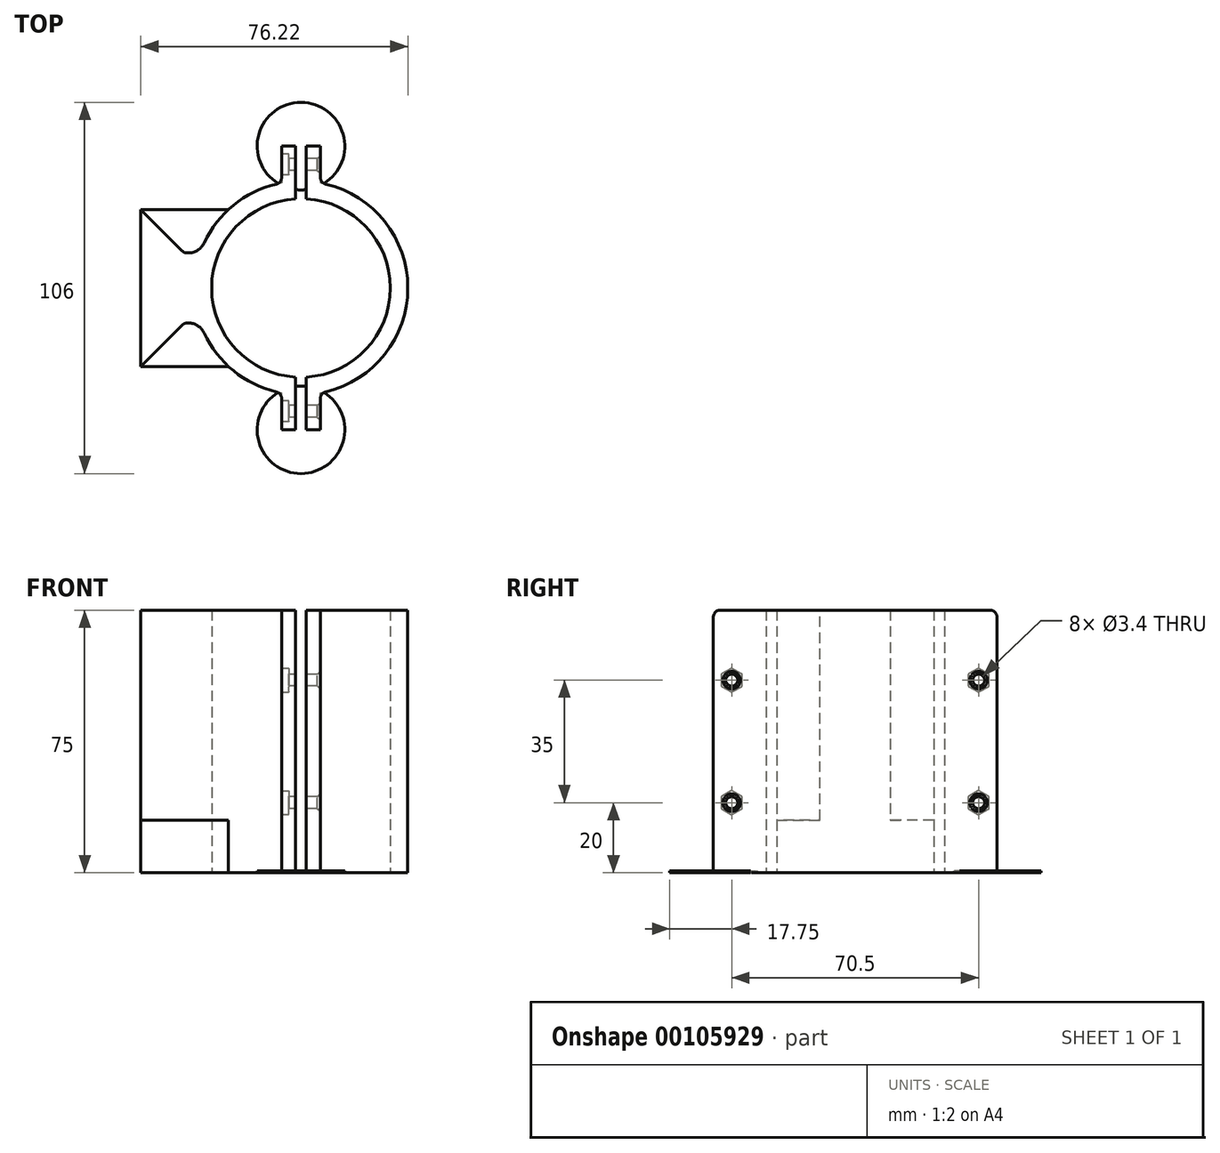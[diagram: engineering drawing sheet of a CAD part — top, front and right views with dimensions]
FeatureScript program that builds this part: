
annotation { "Feature Type Name" : "Feature", "Feature Type Description" : "" }
export const myFeature = defineFeature(function(context is Context, id is Id, definition is map)
    precondition{}
    {
        {
            var Q0;
            Q0=qCreatedBy(makeId("Top.planeOp"),FACE);
            var sketch = newSketch(context, id + "F11", { "sketchPlane" : qUnion([Q0])});
            skLineSegment(sketch, "E0", {"start": v(-5.55, -72.11) * mm, "end": v(110.36, -72.11) * mm, "construction": true});
            skLineSegment(sketch, "E1", {"start": v(-5.55, -72.11) * mm, "end": v(-5.55, -49.71) * mm});
            skLineSegment(sketch, "E2", {"start": v(-5.55, -49.71) * mm, "end": v(6.85, -62.11) * mm});
            skLineSegment(sketch, "E3", {"start": v(6.85, -62.11) * mm, "end": v(11.35, -62.11) * mm});
            skLineSegment(sketch, "E4", {"start": v(11.35, -62.11) * mm, "end": v(11.35, -72.11) * mm});
            skLineSegment(sketch, "E5.MirrorCS", {"start": v(-5.55, -94.51) * mm, "end": v(6.85, -82.11) * mm});
            skLineSegment(sketch, "E6.MirrorCS", {"start": v(11.35, -82.11) * mm, "end": v(11.35, -72.11) * mm});
            skLineSegment(sketch, "E7.MirrorCS", {"start": v(6.85, -82.11) * mm, "end": v(11.35, -82.11) * mm});
            skLineSegment(sketch, "E8.MirrorCS", {"start": v(-5.55, -72.11) * mm, "end": v(-5.55, -94.51) * mm});
            skCircle(sketch, "E9", {"center": v(40.17, -72.11) * mm, "radius": 30.5 * mm});
            skCircle(sketch, "E10.0", {"center": v(40.17, -72.11) * mm, "radius": 25.5 * mm});
            skLineSegment(sketch, "E11", {"start": v(40.17, -31.61) * mm, "end": v(40.17, -110.67) * mm, "construction": true});
            skLineSegment(sketch, "E12", {"start": v(38.67, -31.61) * mm, "end": v(38.67, -46.65) * mm});
            skLineSegment(sketch, "E13", {"start": v(38.67, -31.61) * mm, "end": v(34.67, -31.61) * mm});
            skLineSegment(sketch, "E14", {"start": v(34.67, -31.61) * mm, "end": v(34.67, -47.21) * mm});
            skLineSegment(sketch, "E15.MirrorCS", {"start": v(41.67, -31.61) * mm, "end": v(41.67, -46.65) * mm});
            skLineSegment(sketch, "E16.MirrorCS", {"start": v(45.67, -31.61) * mm, "end": v(45.67, -47.21) * mm});
            skLineSegment(sketch, "E17.MirrorCS", {"start": v(41.67, -31.61) * mm, "end": v(45.67, -31.61) * mm});
            skLineSegment(sketch, "E18.MirrorCS", {"start": v(34.67, -112.61) * mm, "end": v(34.67, -97.01) * mm});
            skLineSegment(sketch, "E19.MirrorCS", {"start": v(41.67, -112.61) * mm, "end": v(45.67, -112.61) * mm});
            skLineSegment(sketch, "E20.MirrorCS", {"start": v(38.67, -112.61) * mm, "end": v(34.67, -112.61) * mm});
            skLineSegment(sketch, "E21.MirrorCS", {"start": v(41.67, -112.61) * mm, "end": v(41.67, -97.57) * mm});
            skLineSegment(sketch, "E22.MirrorCS", {"start": v(45.67, -112.61) * mm, "end": v(45.67, -97.01) * mm});
            skLineSegment(sketch, "E23.MirrorCS", {"start": v(38.67, -112.61) * mm, "end": v(38.67, -97.57) * mm});
            skLineSegment(sketch, "E24", {"start": v(-5.55, -49.71) * mm, "end": v(19.47, -49.71) * mm});
            skLineSegment(sketch, "E25", {"start": v(-5.55, -94.51) * mm, "end": v(19.47, -94.51) * mm});
            skCircle(sketch, "E26", {"center": v(40.17, -31.61) * mm, "radius": 12.5 * mm});
            skCircle(sketch, "E27.MirrorC", {"center": v(40.17, -112.61) * mm, "radius": 12.5 * mm});
            skSolve(sketch);
        }
        {
            var Q0;
            Q0=makeQuery(id+"F11.imprint","IMPRINT",FACE,{"disambiguationData":[TD([[makeQuery(id+"F11.imprint","IMPRINT",EDGE,{"derivedFrom":sQuery(id+"F11.wireOp",EDGE,"E1")}),-1.0]])]});
            var Q1;
            {var subQ0=sQuery(id+"F11.wireOp",EDGE,"E4");Q1=makeQuery(id+"F11.imprint","IMPRINT",FACE,{"disambiguationData":[TD([[makeQuery(id+"F11.imprint","IMPRINT",EDGE,{"derivedFrom":subQ0}),-1.0]])]});}
            var Q2;
            {var subQ10=sQuery(id+"F11.wireOp",EDGE,"E4");Q2=makeQuery(id+"F11.imprint","IMPRINT",FACE,{"disambiguationData":[TD([[makeQuery(id+"F11.imprint","IMPRINT",EDGE,{"derivedFrom":subQ10}),1.0]])]});}
            var Q3;
            {var subQ5=sQuery(id+"F11.wireOp",EDGE,"E13");Q3=makeQuery(id+"F11.imprint","IMPRINT",FACE,{"disambiguationData":[TD([[makeQuery(id+"F11.imprint","IMPRINT",EDGE,{"derivedFrom":subQ5}),1.0]])]});}
            var Q4;
            {var subQ5=sQuery(id+"F11.wireOp",EDGE,"E17.MirrorCS");Q4=makeQuery(id+"F11.imprint","IMPRINT",FACE,{"disambiguationData":[TD([[makeQuery(id+"F11.imprint","IMPRINT",EDGE,{"derivedFrom":subQ5}),-1.0]])]});}
            var Q5;
            {var subQ0=sQuery(id+"F11.wireOp",EDGE,"E12");var subQ3=sQuery(id+"F11.wireOp",EDGE,"E9");var subQ4=makeQuery(id+"F11.imprint","INTERSECT",VERTEX,{"derivedFrom":[subQ3,subQ0]});Q5=makeQuery(id+"F11.imprint","IMPRINT",FACE,{"disambiguationData":[TD([[makeQuery(id+"F11.imprint","IMPRINT",EDGE,{"disambiguationData":[TD([[subQ4,-1.0]])],"derivedFrom":subQ3}),1.0]])]});}
            var Q6;
            {var subQ0=sQuery(id+"F11.wireOp",EDGE,"E16.MirrorCS");var subQ1=sQuery(id+"F11.wireOp",EDGE,"E9");var subQ2=makeQuery(id+"F11.imprint","INTERSECT",VERTEX,{"derivedFrom":[subQ1,subQ0]});Q6=makeQuery(id+"F11.imprint","IMPRINT",FACE,{"disambiguationData":[TD([[makeQuery(id+"F11.imprint","IMPRINT",EDGE,{"disambiguationData":[TD([[subQ2,-1.0]])],"derivedFrom":subQ1}),1.0]])]});}
            var Q7;
            {var subQ0=sQuery(id+"F11.wireOp",EDGE,"E26");var subQ1=sQuery(id+"F11.wireOp",EDGE,"E9");var subQ2=makeQuery(id+"F11.imprint","INTERSECT",VERTEX,{"disambiguationData":[OD(0.0)],"derivedFrom":[subQ1,subQ0]});Q7=makeQuery(id+"F11.imprint","IMPRINT",FACE,{"disambiguationData":[TD([[makeQuery(id+"F11.imprint","IMPRINT",EDGE,{"disambiguationData":[TD([[subQ2,-1.0]])],"derivedFrom":subQ1}),1.0]])]});}
            var Q8;
            {var subQ7=sQuery(id+"F11.wireOp",EDGE,"E26");var subQ9=sQuery(id+"F11.wireOp",EDGE,"E9");var subQ10=makeQuery(id+"F11.imprint","INTERSECT",VERTEX,{"disambiguationData":[OD(0.0)],"derivedFrom":[subQ9,subQ7]});Q8=makeQuery(id+"F11.imprint","IMPRINT",FACE,{"disambiguationData":[TD([[makeQuery(id+"F11.imprint","IMPRINT",EDGE,{"disambiguationData":[TD([[subQ10,1.0]])],"derivedFrom":subQ9}),1.0]])]});}
            var Q9;
            {var subQ0=sQuery(id+"F11.wireOp",EDGE,"E26");var subQ1=sQuery(id+"F11.wireOp",EDGE,"E9");var subQ2=makeQuery(id+"F11.imprint","INTERSECT",VERTEX,{"disambiguationData":[OD(1.0)],"derivedFrom":[subQ1,subQ0]});Q9=makeQuery(id+"F11.imprint","IMPRINT",FACE,{"disambiguationData":[TD([[makeQuery(id+"F11.imprint","IMPRINT",EDGE,{"disambiguationData":[TD([[subQ2,1.0]])],"derivedFrom":subQ1}),1.0]])]});}
            var Q10;
            {var subQ0=sQuery(id+"F11.wireOp",EDGE,"E27.MirrorC");var subQ1=sQuery(id+"F11.wireOp",EDGE,"E9");var subQ2=makeQuery(id+"F11.imprint","INTERSECT",VERTEX,{"disambiguationData":[OD(0.0)],"derivedFrom":[subQ1,subQ0]});Q10=makeQuery(id+"F11.imprint","IMPRINT",FACE,{"disambiguationData":[TD([[makeQuery(id+"F11.imprint","IMPRINT",EDGE,{"disambiguationData":[TD([[subQ2,-1.0]])],"derivedFrom":subQ1}),1.0]])]});}
            var Q11;
            {var subQ3=sQuery(id+"F11.wireOp",EDGE,"E9");var subQ7=sQuery(id+"F11.wireOp",EDGE,"E18.MirrorCS");var subQ9=makeQuery(id+"F11.imprint","INTERSECT",VERTEX,{"derivedFrom":[subQ3,subQ7]});Q11=makeQuery(id+"F11.imprint","IMPRINT",FACE,{"disambiguationData":[TD([[makeQuery(id+"F11.imprint","IMPRINT",EDGE,{"disambiguationData":[TD([[subQ9,-1.0]])],"derivedFrom":subQ3}),1.0]])]});}
            var Q12;
            {var subQ5=sQuery(id+"F11.wireOp",EDGE,"E20.MirrorCS");Q12=makeQuery(id+"F11.imprint","IMPRINT",FACE,{"disambiguationData":[TD([[makeQuery(id+"F11.imprint","IMPRINT",EDGE,{"derivedFrom":subQ5}),-1.0]])]});}
            var Q13;
            {var subQ0=sQuery(id+"F11.wireOp",EDGE,"E27.MirrorC");var subQ1=sQuery(id+"F11.wireOp",EDGE,"E9");var subQ2=makeQuery(id+"F11.imprint","INTERSECT",VERTEX,{"disambiguationData":[OD(1.0)],"derivedFrom":[subQ1,subQ0]});Q13=makeQuery(id+"F11.imprint","IMPRINT",FACE,{"disambiguationData":[TD([[makeQuery(id+"F11.imprint","IMPRINT",EDGE,{"disambiguationData":[TD([[subQ2,1.0]])],"derivedFrom":subQ1}),1.0]])]});}
            var Q14;
            {var subQ1=sQuery(id+"F11.wireOp",EDGE,"E9");var subQ5=sQuery(id+"F11.wireOp",EDGE,"E21.MirrorCS");var subQ8=makeQuery(id+"F11.imprint","INTERSECT",VERTEX,{"derivedFrom":[subQ1,subQ5]});Q14=makeQuery(id+"F11.imprint","IMPRINT",FACE,{"disambiguationData":[TD([[makeQuery(id+"F11.imprint","IMPRINT",EDGE,{"disambiguationData":[TD([[subQ8,-1.0]])],"derivedFrom":subQ1}),1.0]])]});}
            var Q15;
            {var subQ5=sQuery(id+"F11.wireOp",EDGE,"E19.MirrorCS");Q15=makeQuery(id+"F11.imprint","IMPRINT",FACE,{"disambiguationData":[TD([[makeQuery(id+"F11.imprint","IMPRINT",EDGE,{"derivedFrom":subQ5}),1.0]])]});}
            var Q16;
            {var subQ0=sQuery(id+"F11.wireOp",EDGE,"E14");var subQ1=sQuery(id+"F11.wireOp",EDGE,"E10.0");var subQ2=makeQuery(id+"F11.imprint","INTERSECT",VERTEX,{"derivedFrom":[subQ1,subQ0]});Q16=makeQuery(id+"F11.imprint","IMPRINT",FACE,{"disambiguationData":[TD([[makeQuery(id+"F11.imprint","IMPRINT",EDGE,{"disambiguationData":[TD([[subQ2,1.0]])],"derivedFrom":subQ1}),-1.0]])]});}
            var Q17;
            {var subQ0=sQuery(id+"F11.wireOp",EDGE,"E16.MirrorCS");var subQ1=sQuery(id+"F11.wireOp",EDGE,"E10.0");var subQ2=makeQuery(id+"F11.imprint","INTERSECT",VERTEX,{"derivedFrom":[subQ1,subQ0]});Q17=makeQuery(id+"F11.imprint","IMPRINT",FACE,{"disambiguationData":[TD([[makeQuery(id+"F11.imprint","IMPRINT",EDGE,{"disambiguationData":[TD([[subQ2,-1.0]])],"derivedFrom":subQ1}),-1.0]])]});}
            var Q18;
            {var subQ0=sQuery(id+"F11.wireOp",EDGE,"E18.MirrorCS");var subQ1=sQuery(id+"F11.wireOp",EDGE,"E10.0");var subQ2=makeQuery(id+"F11.imprint","INTERSECT",VERTEX,{"derivedFrom":[subQ1,subQ0]});Q18=makeQuery(id+"F11.imprint","IMPRINT",FACE,{"disambiguationData":[TD([[makeQuery(id+"F11.imprint","IMPRINT",EDGE,{"disambiguationData":[TD([[subQ2,-1.0]])],"derivedFrom":subQ1}),-1.0]])]});}
            var Q19;
            {var subQ0=sQuery(id+"F11.wireOp",EDGE,"E22.MirrorCS");var subQ1=sQuery(id+"F11.wireOp",EDGE,"E10.0");var subQ2=makeQuery(id+"F11.imprint","INTERSECT",VERTEX,{"derivedFrom":[subQ1,subQ0]});Q19=makeQuery(id+"F11.imprint","IMPRINT",FACE,{"disambiguationData":[TD([[makeQuery(id+"F11.imprint","IMPRINT",EDGE,{"disambiguationData":[TD([[subQ2,1.0]])],"derivedFrom":subQ1}),-1.0]])]});}
            extrude(context, id + "F0", {"entities" : qUnion([Q0, Q1, Q2, Q3, Q4, Q5, Q6, Q7, Q8, Q9, Q10, Q11, Q12, Q13, Q14, Q15, Q16, Q17, Q18, Q19]), "depth" : 75 * mm});
        }
        {
            var Q0;
            Q0=makeQuery(id+"F11.imprint","IMPRINT",FACE,{"disambiguationData":[TD([[makeQuery(id+"F11.imprint","IMPRINT",EDGE,{"derivedFrom":sQuery(id+"F11.wireOp",EDGE,"E5.MirrorCS")}),-1.0]])]});
            var Q1;
            Q1=makeQuery(id+"F11.imprint","IMPRINT",FACE,{"disambiguationData":[TD([[makeQuery(id+"F11.imprint","IMPRINT",EDGE,{"derivedFrom":sQuery(id+"F11.wireOp",EDGE,"E2")}),1.0]])]});
            extrude(context, id + "F1", {"entities" : qUnion([Q0, Q1]), "operationType" : NewBodyOperationType.ADD, "depth" : 15 * mm});
        }
        {
            var Q0;
            {var subQ9=sQuery(id+"F11.wireOp",EDGE,"E19.MirrorCS");Q0=makeQuery(id+"F11.imprint","IMPRINT",FACE,{"disambiguationData":[TD([[makeQuery(id+"F11.imprint","IMPRINT",EDGE,{"derivedFrom":subQ9}),-1.0]])]});}
            var Q1;
            {var subQ0=sQuery(id+"F11.wireOp",EDGE,"E13");Q1=makeQuery(id+"F11.imprint","IMPRINT",FACE,{"disambiguationData":[TD([[makeQuery(id+"F11.imprint","IMPRINT",EDGE,{"derivedFrom":subQ0}),-1.0]])]});}
            var Q2;
            {var subQ0=sQuery(id+"F11.wireOp",EDGE,"E23.MirrorCS");var subQ1=sQuery(id+"F11.wireOp",EDGE,"E9");var subQ2=makeQuery(id+"F11.imprint","INTERSECT",VERTEX,{"derivedFrom":[subQ1,subQ0]});Q2=makeQuery(id+"F11.imprint","IMPRINT",FACE,{"disambiguationData":[TD([[makeQuery(id+"F11.imprint","IMPRINT",EDGE,{"disambiguationData":[TD([[subQ2,-1.0]])],"derivedFrom":subQ1}),1.0]])]});}
            var Q3;
            {var subQ0=sQuery(id+"F11.wireOp",EDGE,"E15.MirrorCS");var subQ1=sQuery(id+"F11.wireOp",EDGE,"E9");var subQ2=makeQuery(id+"F11.imprint","INTERSECT",VERTEX,{"derivedFrom":[subQ1,subQ0]});Q3=makeQuery(id+"F11.imprint","IMPRINT",FACE,{"disambiguationData":[TD([[makeQuery(id+"F11.imprint","IMPRINT",EDGE,{"disambiguationData":[TD([[subQ2,-1.0]])],"derivedFrom":subQ1}),1.0]])]});}
            extrude(context, id + "F2", {"entities" : qUnion([Q0, Q1, Q2, Q3]), "depth" : 0.5 * mm});
        }
        {
            var Q0;
            Q0=makeQuery(id+"F0.opExtrude","SWEPT_FACE",FACE,{"disambiguationData":[OSD([sQuery(id+"F11.wireOp",EDGE,"E18.MirrorCS")])]});
            var sketch = newSketch(context, id + "F3", { "sketchPlane" : qUnion([Q0])});
            skLineSegment(sketch, "E28", {"start": v(107.36, 72.5) * mm, "end": v(107.36, 37.5) * mm, "construction": true});
            skLineSegment(sketch, "E29", {"start": v(107.36, 37.5) * mm, "end": v(107.36, 2.5) * mm, "construction": true});
            skCircle(sketch, "E30.cCircle", {"center": v(107.36, 55) * mm, "radius": 3 * mm, "construction": true});
            skLineSegment(sketch, "E30.0", {"start": v(104.36, 53.27) * mm, "end": v(104.36, 56.73) * mm});
            skLineSegment(sketch, "E30.1", {"start": v(104.36, 56.73) * mm, "end": v(107.36, 58.46) * mm});
            skLineSegment(sketch, "E30.2", {"start": v(107.36, 58.46) * mm, "end": v(110.36, 56.73) * mm});
            skLineSegment(sketch, "E30.3", {"start": v(110.36, 56.73) * mm, "end": v(110.36, 53.27) * mm});
            skLineSegment(sketch, "E30.4", {"start": v(110.36, 53.27) * mm, "end": v(107.36, 51.54) * mm});
            skLineSegment(sketch, "E30.5", {"start": v(107.36, 51.54) * mm, "end": v(104.36, 53.27) * mm});
            skPoint(sketch, "E30.0.midPoint", {"position": v(104.36, 55) * mm});
            skCircle(sketch, "E31.cCircle", {"center": v(107.36, 20) * mm, "radius": 3 * mm, "construction": true});
            skLineSegment(sketch, "E31.0", {"start": v(104.36, 18.27) * mm, "end": v(104.36, 21.73) * mm});
            skLineSegment(sketch, "E31.1", {"start": v(104.36, 21.73) * mm, "end": v(107.36, 23.46) * mm});
            skLineSegment(sketch, "E31.2", {"start": v(107.36, 23.46) * mm, "end": v(110.36, 21.73) * mm});
            skLineSegment(sketch, "E31.3", {"start": v(110.36, 21.73) * mm, "end": v(110.36, 18.27) * mm});
            skLineSegment(sketch, "E31.4", {"start": v(110.36, 18.27) * mm, "end": v(107.36, 16.54) * mm});
            skLineSegment(sketch, "E31.5", {"start": v(107.36, 16.54) * mm, "end": v(104.36, 18.27) * mm});
            skPoint(sketch, "E31.0.midPoint", {"position": v(104.36, 20) * mm});
            skCircle(sketch, "E32", {"center": v(107.36, 55) * mm, "radius": 1.7 * mm});
            skCircle(sketch, "E33", {"center": v(107.36, 20) * mm, "radius": 1.7 * mm});
            skLineSegment(sketch, "E34", {"start": v(107.36, 75) * mm, "end": v(107.36, 0) * mm, "construction": true});
            skLineSegment(sketch, "E35.0", {"start": v(114.52, 55) * mm, "end": v(100.2, 55) * mm, "construction": true});
            skLineSegment(sketch, "E36.0", {"start": v(114.52, 20) * mm, "end": v(100.2, 20) * mm, "construction": true});
            skLineSegment(sketch, "E37", {"start": v(36.86, 72.5) * mm, "end": v(36.86, 37.5) * mm, "construction": true});
            skLineSegment(sketch, "E38", {"start": v(36.86, 37.5) * mm, "end": v(36.86, 2.5) * mm, "construction": true});
            skCircle(sketch, "E39.cCircle", {"center": v(36.86, 55) * mm, "radius": 3 * mm, "construction": true});
            skLineSegment(sketch, "E39.0", {"start": v(33.86, 53.27) * mm, "end": v(33.86, 56.73) * mm});
            skLineSegment(sketch, "E39.1", {"start": v(33.86, 56.73) * mm, "end": v(36.86, 58.46) * mm});
            skLineSegment(sketch, "E39.2", {"start": v(36.86, 58.46) * mm, "end": v(39.86, 56.73) * mm});
            skLineSegment(sketch, "E39.3", {"start": v(39.86, 56.73) * mm, "end": v(39.86, 53.27) * mm});
            skLineSegment(sketch, "E39.4", {"start": v(39.86, 53.27) * mm, "end": v(36.86, 51.54) * mm});
            skLineSegment(sketch, "E39.5", {"start": v(36.86, 51.54) * mm, "end": v(33.86, 53.27) * mm});
            skPoint(sketch, "E39.0.midPoint", {"position": v(33.86, 55) * mm});
            skCircle(sketch, "E40.cCircle", {"center": v(36.86, 20) * mm, "radius": 3 * mm, "construction": true});
            skLineSegment(sketch, "E40.0", {"start": v(33.86, 18.27) * mm, "end": v(33.86, 21.73) * mm});
            skLineSegment(sketch, "E40.1", {"start": v(33.86, 21.73) * mm, "end": v(36.86, 23.46) * mm});
            skLineSegment(sketch, "E40.2", {"start": v(36.86, 23.46) * mm, "end": v(39.86, 21.73) * mm});
            skLineSegment(sketch, "E40.3", {"start": v(39.86, 21.73) * mm, "end": v(39.86, 18.27) * mm});
            skLineSegment(sketch, "E40.4", {"start": v(39.86, 18.27) * mm, "end": v(36.86, 16.54) * mm});
            skLineSegment(sketch, "E40.5", {"start": v(36.86, 16.54) * mm, "end": v(33.86, 18.27) * mm});
            skPoint(sketch, "E40.0.midPoint", {"position": v(33.86, 20) * mm});
            skCircle(sketch, "E41", {"center": v(36.86, 55) * mm, "radius": 1.7 * mm});
            skCircle(sketch, "E42", {"center": v(36.86, 20) * mm, "radius": 1.7 * mm});
            skLineSegment(sketch, "E43", {"start": v(36.86, 94.5) * mm, "end": v(36.86, -5.5) * mm, "construction": true});
            skLineSegment(sketch, "E44.0", {"start": v(45.3, 55) * mm, "end": v(28.43, 55) * mm, "construction": true});
            skLineSegment(sketch, "E45.0", {"start": v(43.63, 20) * mm, "end": v(30.1, 20) * mm, "construction": true});
            skLineSegment(sketch, "E46.0", {"start": v(31.61, 70) * mm, "end": v(42.11, 70) * mm, "construction": true});
            skPoint(sketch, "E47", {"position": v(36.86, 70) * mm});
            skSolve(sketch);
        }
        {
            var Q0;
            Q0=qSketchRegion(id+"F3",true);
            extrude(context, id + "F4", {"entities" : qUnion([Q0]), "operationType" : NewBodyOperationType.REMOVE, "oppositeDirection" : true, "depth" : 2 * mm});
        }
        {
            var Q0;
            Q0=makeQuery(id+"F4.boolean.opBoolean","SPLIT",FACE,{"disambiguationData":[TD([makeQuery(id+"F4.opExtrude","SWEPT_FACE",FACE,{"disambiguationData":[OSD([sQuery(id+"F3.wireOp",EDGE,"E41")])]})])],"derivedFrom":makeQuery(id+"F0.opExtrude","SWEPT_FACE",FACE,{"disambiguationData":[OSD([sQuery(id+"F11.wireOp",EDGE,"E14")])]})});
            var Q1;
            Q1=makeQuery(id+"F4.boolean.opBoolean","SPLIT",FACE,{"disambiguationData":[TD([makeQuery(id+"F4.opExtrude","SWEPT_FACE",FACE,{"disambiguationData":[OSD([sQuery(id+"F3.wireOp",EDGE,"E32")])]})])],"derivedFrom":makeQuery(id+"F0.opExtrude","SWEPT_FACE",FACE,{"disambiguationData":[OSD([sQuery(id+"F11.wireOp",EDGE,"E18.MirrorCS")])]})});
            var Q2;
            Q2=makeQuery(id+"F4.boolean.opBoolean","SPLIT",FACE,{"disambiguationData":[TD([makeQuery(id+"F4.opExtrude","SWEPT_FACE",FACE,{"disambiguationData":[OSD([sQuery(id+"F3.wireOp",EDGE,"E33")])]})])],"derivedFrom":makeQuery(id+"F0.opExtrude","SWEPT_FACE",FACE,{"disambiguationData":[OSD([sQuery(id+"F11.wireOp",EDGE,"E18.MirrorCS")])]})});
            var Q3;
            Q3=makeQuery(id+"F4.boolean.opBoolean","SPLIT",FACE,{"disambiguationData":[TD([makeQuery(id+"F4.opExtrude","SWEPT_FACE",FACE,{"disambiguationData":[OSD([sQuery(id+"F3.wireOp",EDGE,"E42")])]})])],"derivedFrom":makeQuery(id+"F0.opExtrude","SWEPT_FACE",FACE,{"disambiguationData":[OSD([sQuery(id+"F11.wireOp",EDGE,"E14")])]})});
            var Q4;
            Q4=makeQuery(id+"F0.opExtrude","SWEPT_FACE",FACE,{"disambiguationData":[OSD([sQuery(id+"F11.wireOp",EDGE,"E16.MirrorCS")])]});
            var Q5;
            Q5=makeQuery(id+"F0.opExtrude","SWEPT_BODY",BODY,{"disambiguationData":[OSD([sQuery(id+"F11.wireOp",EDGE,"E9"),sQuery(id+"F11.wireOp",EDGE,"E10.0"),sQuery(id+"F11.wireOp",EDGE,"E15.MirrorCS"),sQuery(id+"F11.wireOp",EDGE,"E16.MirrorCS"),sQuery(id+"F11.wireOp",EDGE,"E17.MirrorCS"),sQuery(id+"F11.wireOp",EDGE,"E19.MirrorCS"),sQuery(id+"F11.wireOp",EDGE,"E21.MirrorCS"),sQuery(id+"F11.wireOp",EDGE,"E22.MirrorCS")])]});
            extrude(context, id + "F5", {"entities" : qUnion([Q0, Q1, Q2, Q3]), "operationType" : NewBodyOperationType.REMOVE, "endBound" : BoundingType.THROUGH_ALL, "oppositeDirection" : true, "endBoundEntityFace" : qUnion([Q4]), "endBoundEntityBody" : qUnion([Q5]), "depth" : 46.64 * mm});
        }
        {
            var Q0;
            Q0=makeQuery(id+"F5.boolean.opBoolean","INTERSECT",EDGE,{"derivedFrom":[makeQuery(id+"F0.opExtrude","SWEPT_FACE",FACE,{"disambiguationData":[OSD([sQuery(id+"F11.wireOp",EDGE,"E22.MirrorCS")])]}),makeQuery(id+"F5.opExtrude","SWEPT_FACE",FACE,{"disambiguationData":[OSD([sQuery(id+"F3.wireOp",EDGE,"E33")])]})]});
            var Q1;
            Q1=makeQuery(id+"F5.boolean.opBoolean","INTERSECT",EDGE,{"derivedFrom":[makeQuery(id+"F0.opExtrude","SWEPT_FACE",FACE,{"disambiguationData":[OSD([sQuery(id+"F11.wireOp",EDGE,"E22.MirrorCS")])]}),makeQuery(id+"F5.opExtrude","SWEPT_FACE",FACE,{"disambiguationData":[OSD([sQuery(id+"F3.wireOp",EDGE,"E32")])]})]});
            var Q2;
            Q2=makeQuery(id+"F5.boolean.opBoolean","INTERSECT",EDGE,{"derivedFrom":[makeQuery(id+"F0.opExtrude","SWEPT_FACE",FACE,{"disambiguationData":[OSD([sQuery(id+"F11.wireOp",EDGE,"E16.MirrorCS")])]}),makeQuery(id+"F5.opExtrude","SWEPT_FACE",FACE,{"disambiguationData":[OSD([sQuery(id+"F3.wireOp",EDGE,"E41")])]})]});
            var Q3;
            Q3=makeQuery(id+"F5.boolean.opBoolean","INTERSECT",EDGE,{"derivedFrom":[makeQuery(id+"F0.opExtrude","SWEPT_FACE",FACE,{"disambiguationData":[OSD([sQuery(id+"F11.wireOp",EDGE,"E16.MirrorCS")])]}),makeQuery(id+"F5.opExtrude","SWEPT_FACE",FACE,{"disambiguationData":[OSD([sQuery(id+"F3.wireOp",EDGE,"E42")])]})]});
            chamfer(context, id + "F6", {"entities" : qUnion([Q0, Q1, Q2, Q3]), "width" : 0.8 * mm, "tangentPropagation" : true});
        }
        {
            var Q0;
            Q0=makeQuery(id+"F0.opExtrude","SWEPT_EDGE",EDGE,{"disambiguationData":[OSD([sQuery(id+"F11.wireOp",EDGE,"E9"),sQuery(id+"F11.wireOp",EDGE,"E22.MirrorCS")])]});
            var Q1;
            Q1=makeQuery(id+"F0.opExtrude","SWEPT_EDGE",EDGE,{"disambiguationData":[OSD([sQuery(id+"F11.wireOp",EDGE,"E9"),sQuery(id+"F11.wireOp",EDGE,"E16.MirrorCS")])]});
            var Q2;
            Q2=makeQuery(id+"F0.opExtrude","SWEPT_EDGE",EDGE,{"disambiguationData":[OSD([sQuery(id+"F11.wireOp",EDGE,"E9"),sQuery(id+"F11.wireOp",EDGE,"E14")])]});
            var Q3;
            Q3=makeQuery(id+"F0.opExtrude","SWEPT_EDGE",EDGE,{"disambiguationData":[OSD([sQuery(id+"F11.wireOp",EDGE,"E9"),sQuery(id+"F11.wireOp",EDGE,"E18.MirrorCS")])]});
            var Q4;
            Q4=makeQuery(id+"F0.opExtrude","SWEPT_EDGE",EDGE,{"disambiguationData":[OSD([sQuery(id+"F11.wireOp",EDGE,"E5.MirrorCS"),sQuery(id+"F11.wireOp",EDGE,"E7.MirrorCS")])]});
            var Q5;
            Q5=makeQuery(id+"F0.opExtrude","SWEPT_EDGE",EDGE,{"disambiguationData":[OSD([sQuery(id+"F11.wireOp",EDGE,"E2"),sQuery(id+"F11.wireOp",EDGE,"E3")])]});
            fillet(context, id + "F7", {"entities" : qUnion([Q0, Q1, Q2, Q3, Q4, Q5]), "radius" : 2 * mm, "tangentPropagation" : true, "allowEdgeOverflow" : false});
        }
        {
            var Q0;
            Q0=makeQuery(id+"F0.opExtrude","SWEPT_EDGE",EDGE,{"disambiguationData":[OSD([sQuery(id+"F11.wireOp",EDGE,"E3"),sQuery(id+"F11.wireOp",EDGE,"E4"),sQuery(id+"F11.wireOp",EDGE,"E9")])]});
            var Q1;
            Q1=makeQuery(id+"F0.opExtrude","SWEPT_EDGE",EDGE,{"disambiguationData":[OSD([sQuery(id+"F11.wireOp",EDGE,"E6.MirrorCS"),sQuery(id+"F11.wireOp",EDGE,"E7.MirrorCS"),sQuery(id+"F11.wireOp",EDGE,"E9")])]});
            fillet(context, id + "F8", {"entities" : qUnion([Q0, Q1]), "radius" : 5 * mm, "tangentPropagation" : true, "allowEdgeOverflow" : false});
        }
        {
            var Q0;
            Q0=makeQuery(id+"F4.boolean.opBoolean","COPY",EDGE,{"derivedFrom":makeQuery(id+"F4.opExtrude","SWEPT_EDGE",EDGE,{"disambiguationData":[OSD([sQuery(id+"F3.wireOp",EDGE,"E39.0"),sQuery(id+"F3.wireOp",EDGE,"E39.5")])]})});
            var Q1;
            Q1=makeQuery(id+"F4.boolean.opBoolean","COPY",EDGE,{"derivedFrom":makeQuery(id+"F4.opExtrude","SWEPT_EDGE",EDGE,{"disambiguationData":[OSD([sQuery(id+"F3.wireOp",EDGE,"E39.4"),sQuery(id+"F3.wireOp",EDGE,"E39.5")])]})});
            var Q2;
            Q2=makeQuery(id+"F4.boolean.opBoolean","COPY",EDGE,{"derivedFrom":makeQuery(id+"F4.opExtrude","SWEPT_EDGE",EDGE,{"disambiguationData":[OSD([sQuery(id+"F3.wireOp",EDGE,"E39.1"),sQuery(id+"F3.wireOp",EDGE,"E39.2")])]})});
            var Q3;
            Q3=makeQuery(id+"F4.boolean.opBoolean","COPY",EDGE,{"derivedFrom":makeQuery(id+"F4.opExtrude","SWEPT_EDGE",EDGE,{"disambiguationData":[OSD([sQuery(id+"F3.wireOp",EDGE,"E39.2"),sQuery(id+"F3.wireOp",EDGE,"E39.3")])]})});
            var Q4;
            Q4=makeQuery(id+"F4.boolean.opBoolean","COPY",EDGE,{"derivedFrom":makeQuery(id+"F4.opExtrude","SWEPT_EDGE",EDGE,{"disambiguationData":[OSD([sQuery(id+"F3.wireOp",EDGE,"E39.3"),sQuery(id+"F3.wireOp",EDGE,"E39.4")])]})});
            var Q5;
            Q5=makeQuery(id+"F4.boolean.opBoolean","COPY",EDGE,{"derivedFrom":makeQuery(id+"F4.opExtrude","SWEPT_EDGE",EDGE,{"disambiguationData":[OSD([sQuery(id+"F3.wireOp",EDGE,"E39.0"),sQuery(id+"F3.wireOp",EDGE,"E39.1")])]})});
            var Q6;
            Q6=makeQuery(id+"F4.boolean.opBoolean","COPY",EDGE,{"derivedFrom":makeQuery(id+"F4.opExtrude","SWEPT_EDGE",EDGE,{"disambiguationData":[OSD([sQuery(id+"F3.wireOp",EDGE,"E30.0"),sQuery(id+"F3.wireOp",EDGE,"E30.1")])]})});
            var Q7;
            Q7=makeQuery(id+"F4.boolean.opBoolean","COPY",EDGE,{"derivedFrom":makeQuery(id+"F4.opExtrude","SWEPT_EDGE",EDGE,{"disambiguationData":[OSD([sQuery(id+"F3.wireOp",EDGE,"E30.1"),sQuery(id+"F3.wireOp",EDGE,"E30.2")])]})});
            var Q8;
            Q8=makeQuery(id+"F4.boolean.opBoolean","COPY",EDGE,{"derivedFrom":makeQuery(id+"F4.opExtrude","SWEPT_EDGE",EDGE,{"disambiguationData":[OSD([sQuery(id+"F3.wireOp",EDGE,"E30.0"),sQuery(id+"F3.wireOp",EDGE,"E30.5")])]})});
            var Q9;
            Q9=makeQuery(id+"F4.boolean.opBoolean","COPY",EDGE,{"derivedFrom":makeQuery(id+"F4.opExtrude","SWEPT_EDGE",EDGE,{"disambiguationData":[OSD([sQuery(id+"F3.wireOp",EDGE,"E30.4"),sQuery(id+"F3.wireOp",EDGE,"E30.5")])]})});
            var Q10;
            Q10=makeQuery(id+"F4.boolean.opBoolean","COPY",EDGE,{"derivedFrom":makeQuery(id+"F4.opExtrude","SWEPT_EDGE",EDGE,{"disambiguationData":[OSD([sQuery(id+"F3.wireOp",EDGE,"E30.3"),sQuery(id+"F3.wireOp",EDGE,"E30.4")])]})});
            var Q11;
            Q11=makeQuery(id+"F4.boolean.opBoolean","COPY",EDGE,{"derivedFrom":makeQuery(id+"F4.opExtrude","SWEPT_EDGE",EDGE,{"disambiguationData":[OSD([sQuery(id+"F3.wireOp",EDGE,"E30.2"),sQuery(id+"F3.wireOp",EDGE,"E30.3")])]})});
            var Q12;
            Q12=makeQuery(id+"F4.boolean.opBoolean","COPY",EDGE,{"derivedFrom":makeQuery(id+"F4.opExtrude","SWEPT_EDGE",EDGE,{"disambiguationData":[OSD([sQuery(id+"F3.wireOp",EDGE,"E31.0"),sQuery(id+"F3.wireOp",EDGE,"E31.1")])]})});
            var Q13;
            Q13=makeQuery(id+"F4.boolean.opBoolean","COPY",EDGE,{"derivedFrom":makeQuery(id+"F4.opExtrude","SWEPT_EDGE",EDGE,{"disambiguationData":[OSD([sQuery(id+"F3.wireOp",EDGE,"E31.0"),sQuery(id+"F3.wireOp",EDGE,"E31.5")])]})});
            var Q14;
            Q14=makeQuery(id+"F4.boolean.opBoolean","COPY",EDGE,{"derivedFrom":makeQuery(id+"F4.opExtrude","SWEPT_EDGE",EDGE,{"disambiguationData":[OSD([sQuery(id+"F3.wireOp",EDGE,"E31.1"),sQuery(id+"F3.wireOp",EDGE,"E31.2")])]})});
            var Q15;
            Q15=makeQuery(id+"F4.boolean.opBoolean","COPY",EDGE,{"derivedFrom":makeQuery(id+"F4.opExtrude","SWEPT_EDGE",EDGE,{"disambiguationData":[OSD([sQuery(id+"F3.wireOp",EDGE,"E31.2"),sQuery(id+"F3.wireOp",EDGE,"E31.3")])]})});
            var Q16;
            Q16=makeQuery(id+"F4.boolean.opBoolean","COPY",EDGE,{"derivedFrom":makeQuery(id+"F4.opExtrude","SWEPT_EDGE",EDGE,{"disambiguationData":[OSD([sQuery(id+"F3.wireOp",EDGE,"E31.3"),sQuery(id+"F3.wireOp",EDGE,"E31.4")])]})});
            var Q17;
            Q17=makeQuery(id+"F4.boolean.opBoolean","COPY",EDGE,{"derivedFrom":makeQuery(id+"F4.opExtrude","SWEPT_EDGE",EDGE,{"disambiguationData":[OSD([sQuery(id+"F3.wireOp",EDGE,"E31.4"),sQuery(id+"F3.wireOp",EDGE,"E31.5")])]})});
            var Q18;
            Q18=makeQuery(id+"F4.boolean.opBoolean","COPY",EDGE,{"derivedFrom":makeQuery(id+"F4.opExtrude","SWEPT_EDGE",EDGE,{"disambiguationData":[OSD([sQuery(id+"F3.wireOp",EDGE,"E40.4"),sQuery(id+"F3.wireOp",EDGE,"E40.5")])]})});
            var Q19;
            Q19=makeQuery(id+"F4.boolean.opBoolean","COPY",EDGE,{"derivedFrom":makeQuery(id+"F4.opExtrude","SWEPT_EDGE",EDGE,{"disambiguationData":[OSD([sQuery(id+"F3.wireOp",EDGE,"E40.0"),sQuery(id+"F3.wireOp",EDGE,"E40.5")])]})});
            var Q20;
            Q20=makeQuery(id+"F4.boolean.opBoolean","COPY",EDGE,{"derivedFrom":makeQuery(id+"F4.opExtrude","SWEPT_EDGE",EDGE,{"disambiguationData":[OSD([sQuery(id+"F3.wireOp",EDGE,"E40.0"),sQuery(id+"F3.wireOp",EDGE,"E40.1")])]})});
            var Q21;
            Q21=makeQuery(id+"F4.boolean.opBoolean","COPY",EDGE,{"derivedFrom":makeQuery(id+"F4.opExtrude","SWEPT_EDGE",EDGE,{"disambiguationData":[OSD([sQuery(id+"F3.wireOp",EDGE,"E40.1"),sQuery(id+"F3.wireOp",EDGE,"E40.2")])]})});
            var Q22;
            Q22=makeQuery(id+"F4.boolean.opBoolean","COPY",EDGE,{"derivedFrom":makeQuery(id+"F4.opExtrude","SWEPT_EDGE",EDGE,{"disambiguationData":[OSD([sQuery(id+"F3.wireOp",EDGE,"E40.3"),sQuery(id+"F3.wireOp",EDGE,"E40.4")])]})});
            var Q23;
            Q23=makeQuery(id+"F4.boolean.opBoolean","COPY",EDGE,{"derivedFrom":makeQuery(id+"F4.opExtrude","SWEPT_EDGE",EDGE,{"disambiguationData":[OSD([sQuery(id+"F3.wireOp",EDGE,"E40.2"),sQuery(id+"F3.wireOp",EDGE,"E40.3")])]})});
            fillet(context, id + "F9", {"entities" : qUnion([Q0, Q1, Q2, Q3, Q4, Q5, Q6, Q7, Q8, Q9, Q10, Q11, Q12, Q13, Q14, Q15, Q16, Q17, Q18, Q19, Q20, Q21, Q22, Q23]), "radius" : 0.4 * mm, "tangentPropagation" : true, "allowEdgeOverflow" : false});
        }
        {
            var Q0;
            Q0=makeQuery(id+"F0.opExtrude","CAP_EDGE",EDGE,{"disambiguationData":[OSD([sQuery(id+"F11.wireOp",EDGE,"E17.MirrorCS")])],"isStart":false});
            var Q1;
            Q1=makeQuery(id+"F0.opExtrude","CAP_EDGE",EDGE,{"disambiguationData":[OSD([sQuery(id+"F11.wireOp",EDGE,"E13")])],"isStart":false});
            var Q2;
            Q2=makeQuery(id+"F0.opExtrude","CAP_EDGE",EDGE,{"disambiguationData":[OSD([sQuery(id+"F11.wireOp",EDGE,"E20.MirrorCS")])],"isStart":false});
            var Q3;
            Q3=makeQuery(id+"F0.opExtrude","CAP_EDGE",EDGE,{"disambiguationData":[OSD([sQuery(id+"F11.wireOp",EDGE,"E19.MirrorCS")])],"isStart":false});
            fillet(context, id + "F10", {"entities" : qUnion([Q0, Q1, Q2, Q3]), "radius" : 2 * mm, "tangentPropagation" : true, "allowEdgeOverflow" : false});
        }
    });
